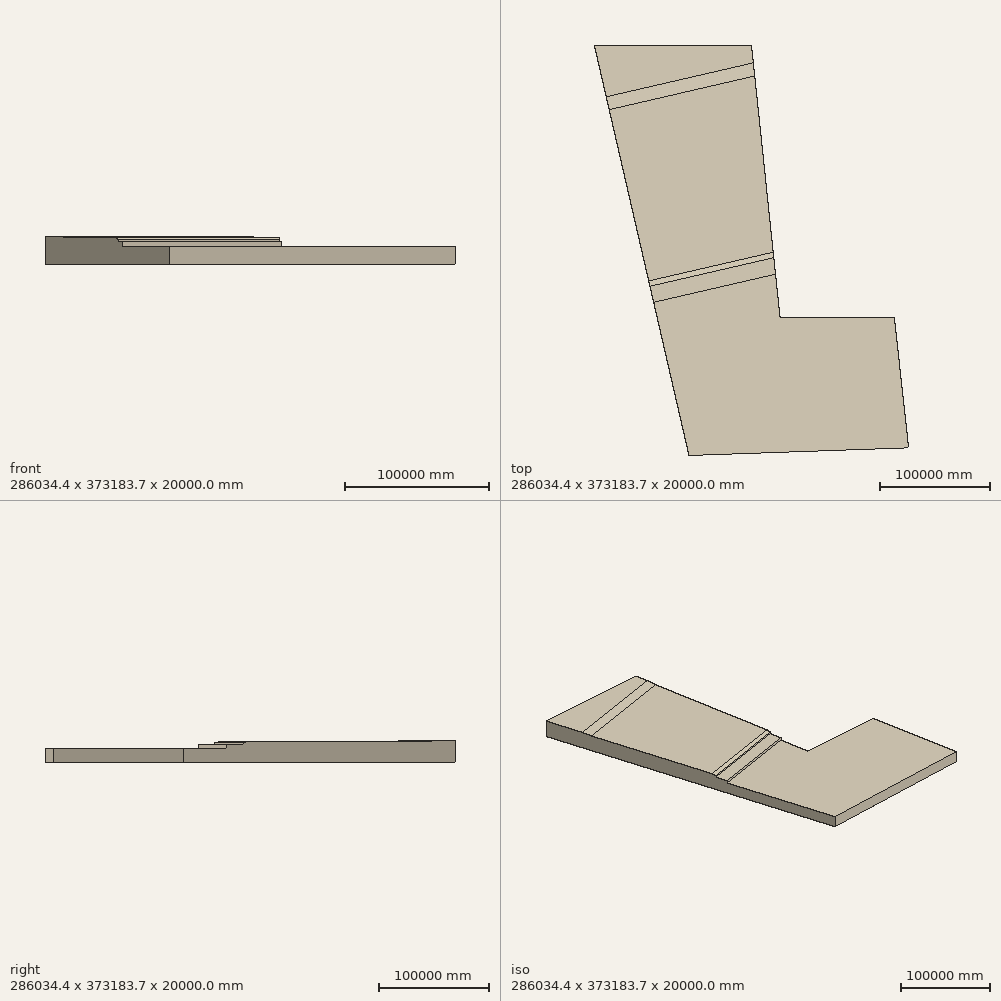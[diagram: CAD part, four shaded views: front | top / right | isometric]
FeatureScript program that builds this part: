
annotation { "Feature Type Name" : "Feature", "Feature Type Description" : "" }
export const myFeature = defineFeature(function(context is Context, id is Id, definition is map)
    precondition{}
    {
        {
            var Q0;
            Q0=qCreatedBy(makeId("Top.planeOp"),FACE);
            var sketch = newSketch(context, id + "F0", { "sketchPlane" : qUnion([Q0])});
            skLineSegment(sketch, "E0", {"start": v(-103886.94, 125755.7) * mm, "end": v(39113.06, 125755.7) * mm});
            skLineSegment(sketch, "E1", {"start": v(65140.65, -121880.25) * mm, "end": v(169140.65, -121880.25) * mm});
            skLineSegment(sketch, "E2", {"start": v(169140.65, -121880.25) * mm, "end": v(182147.48, -240448.13) * mm});
            skLineSegment(sketch, "E3", {"start": v(182147.48, -240448.13) * mm, "end": v(-17730.68, -247428.03) * mm});
            skLineSegment(sketch, "E4", {"start": v(-17730.68, -247428.03) * mm, "end": v(-103886.94, 125755.7) * mm});
            skLineSegment(sketch, "E5", {"start": v(39113.06, 125755.7) * mm, "end": v(65140.65, -121880.25) * mm});
            skSolve(sketch);
        }
        {
            var Q0;
            Q0 = qSketchRegion(id + "F0", true);
            extrude(context, id + "F1", {"entities" : qUnion([Q0]), "depth" : 20000 * mm});
        }
        {
            var Q0;
            Q0=makeQuery(id+"F1.opExtrude","SWEPT_FACE",FACE,{"disambiguationData":[OSD([sQuery(id+"F0.wireOp",EDGE,"E4")])]});
            var sketch = newSketch(context, id + "F2", { "sketchPlane" : qUnion([Q0])});
            skLineSegment(sketch, "E6", {"start": v(-145902.07, 20000) * mm, "end": v(-97902.07, 20000) * mm});
            skLineSegment(sketch, "E7", {"start": v(-97902.07, 20000) * mm, "end": v(-85902.07, 19000) * mm});
            skLineSegment(sketch, "E8", {"start": v(-85902.07, 19000) * mm, "end": v(74097.93, 19000) * mm});
            skLineSegment(sketch, "E9", {"start": v(74097.93, 19000) * mm, "end": v(79097.93, 18000) * mm});
            skLineSegment(sketch, "E10", {"start": v(79097.93, 18000) * mm, "end": v(79097.93, 16000) * mm});
            skLineSegment(sketch, "E11", {"start": v(79097.93, 16000) * mm, "end": v(94097.93, 16000) * mm});
            skLineSegment(sketch, "E12", {"start": v(94097.93, 16000) * mm, "end": v(94097.93, 13000) * mm});
            skLineSegment(sketch, "E13", {"start": v(94097.93, 13000) * mm, "end": v(237097.93, 13000) * mm});
            skLineSegment(sketch, "E14", {"start": v(237097.93, 13000) * mm, "end": v(277097.93, 13000) * mm});
            skLineSegment(sketch, "E15", {"start": v(277097.93, 13000) * mm, "end": v(277097.93, 35466.81) * mm});
            skLineSegment(sketch, "E16", {"start": v(277097.93, 35466.81) * mm, "end": v(-182850.4, 35466.81) * mm});
            skLineSegment(sketch, "E17", {"start": v(-182850.4, 35466.81) * mm, "end": v(-182850.4, 23032.69) * mm});
            skLineSegment(sketch, "E18", {"start": v(-182850.4, 23032.69) * mm, "end": v(-145902.07, 20000) * mm});
            skSolve(sketch);
        }
        {
            var Q0;
            Q0 = qSketchRegion(id + "F2", true);
            extrude(context, id + "F3", {"entities" : qUnion([Q0]), "operationType" : NewBodyOperationType.REMOVE, "oppositeDirection" : true, "depth" : 230000 * mm});
        }
    });
